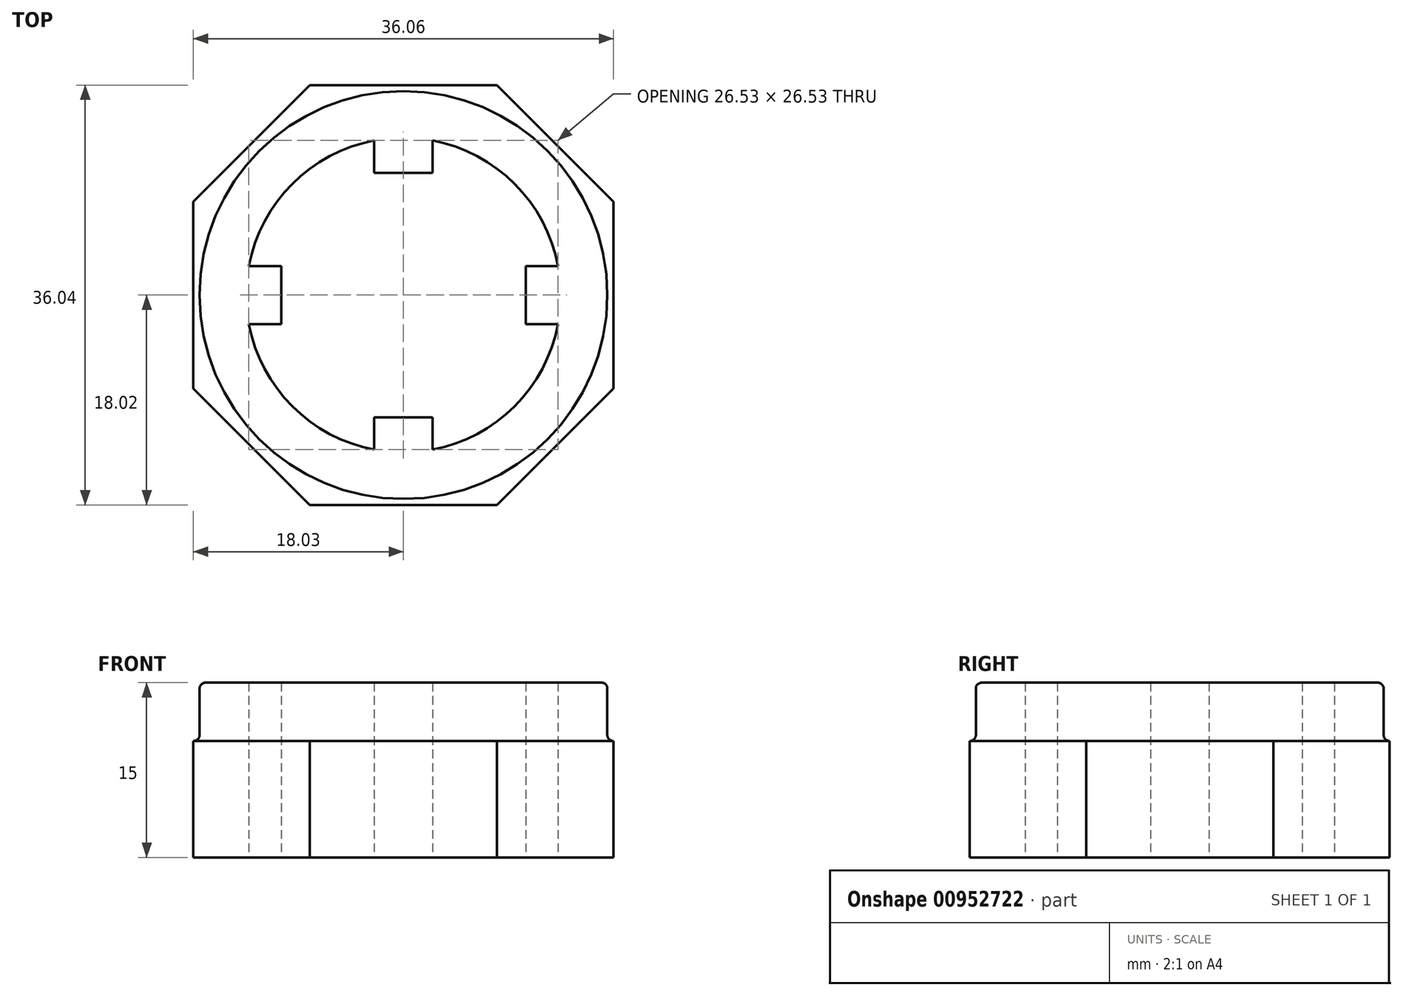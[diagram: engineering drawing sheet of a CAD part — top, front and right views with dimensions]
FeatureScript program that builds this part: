
annotation { "Feature Type Name" : "Feature", "Feature Type Description" : "" }
export const myFeature = defineFeature(function(context is Context, id is Id, definition is map)
    precondition{}
    {
        {
            var Q0;
            Q0=qCreatedBy(makeId("Top.planeOp"),FACE);
            var sketch = newSketch(context, id + "F0", { "sketchPlane" : qUnion([Q0])});
            skCircle(sketch, "E0", {"center": v(0, 0) * mm, "radius": 13.5 * mm});
            skSolve(sketch);
        }
        {
            var Q0;
            Q0=makeQuery(id+"F0.imprint","IMPRINT",FACE,{"disambiguationData":[TD([[makeQuery(id+"F0.imprint","IMPRINT",EDGE,{"derivedFrom":sQuery(id+"F0.wireOp",EDGE,"E0")}),1.0]])]});
            var sketch = newSketch(context, id + "F1", { "sketchPlane" : qUnion([Q0])});
            skCircle(sketch, "E1", {"center": v(0, 0) * mm, "radius": 17.5 * mm});
            skSolve(sketch);
        }
        {
            var Q0;
            Q0=makeQuery(id+"F1.imprint","IMPRINT",FACE,{"disambiguationData":[TD([[makeQuery(id+"F1.imprint","IMPRINT",EDGE,{"derivedFrom":sQuery(id+"F1.wireOp",EDGE,"E1")}),1.0]])]});
            var Q1;
            Q1=sQuery(id+"F1.wireOp",EDGE,"E1");
            extrude(context, id + "F2", {"entities" : qUnion([Q0]), "surfaceEntities" : qUnion([Q1]), "depth" : 15 * mm, "offsetDistance" : 25 * mm});
        }
        {
            var Q0;
            Q0=makeQuery(id+"F0.imprint","IMPRINT",FACE,{"disambiguationData":[TD([[makeQuery(id+"F0.imprint","IMPRINT",EDGE,{"derivedFrom":sQuery(id+"F0.wireOp",EDGE,"E0")}),1.0]])]});
            var sketch = newSketch(context, id + "F3", { "sketchPlane" : qUnion([Q0])});
            skCircle(sketch, "E2", {"center": v(0, 0) * mm, "radius": 10.5 * mm});
            skSolve(sketch);
        }
        {
            var Q0;
            Q0=qCreatedBy(makeId("Top.planeOp"),FACE);
            var sketch = newSketch(context, id + "F4", { "sketchPlane" : qUnion([Q0])});
            skLineSegment(sketch, "E3.bottom", {"start": v(-2.5, 14.36) * mm, "end": v(2.5, 14.36) * mm});
            skLineSegment(sketch, "E3.top", {"start": v(-2.5, 10.5) * mm, "end": v(2.5, 10.5) * mm});
            skLineSegment(sketch, "E3.left", {"start": v(-2.5, 14.36) * mm, "end": v(-2.5, 10.5) * mm});
            skLineSegment(sketch, "E3.right", {"start": v(2.5, 14.36) * mm, "end": v(2.5, 10.5) * mm});
            skSolve(sketch);
        }
        {
            var Q0;
            Q0=makeQuery(id+"F4.imprint","IMPRINT",FACE,{"disambiguationData":[TD([[makeQuery(id+"F4.imprint","IMPRINT",EDGE,{"derivedFrom":sQuery(id+"F4.wireOp",EDGE,"E3.bottom")}),-1.0]])]});
            var Q1;
            Q1=sQuery(id+"F4.wireOp",EDGE,"E3.left");
            var Q2;
            Q2=sQuery(id+"F4.wireOp",EDGE,"E3.right");
            var Q3;
            Q3=sQuery(id+"F4.wireOp",EDGE,"E3.bottom");
            var Q4;
            Q4=sQuery(id+"F4.wireOp",EDGE,"E3.top");
            extrude(context, id + "F5", {"entities" : qUnion([Q0]), "operationType" : NewBodyOperationType.ADD, "surfaceEntities" : qUnion([Q1, Q2, Q3, Q4]), "depth" : 15 * mm, "offsetDistance" : 25 * mm});
        }
        {
            var Q0;
            Q0=makeQuery(id+"F2.opExtrude","SWEPT_BODY",BODY,{"disambiguationData":[OSD([sQuery(id+"F0.wireOp",EDGE,"E0"),sQuery(id+"F1.wireOp",EDGE,"E1")])]});
            var Q1;
            Q1=sQuery(id+"F3.wireOp",EDGE,"E2");
            circularPattern(context, id + "F6", {"operationType" : NewBodyOperationType.ADD, "entities" : qUnion([Q0]), "axis" : qUnion([Q1]), "angle" : 360 * degree, "instanceCount" : 4, "equalSpace" : true});
        }
        {
            var Q0;
            Q0=makeQuery(id+"F0.imprint","IMPRINT",FACE,{"disambiguationData":[TD([[makeQuery(id+"F0.imprint","IMPRINT",EDGE,{"derivedFrom":sQuery(id+"F0.wireOp",EDGE,"E0")}),1.0]])]});
            var sketch = newSketch(context, id + "F7", { "sketchPlane" : qUnion([Q0])});
            skLineSegment(sketch, "E4.bottom", {"start": v(18.03, -18.02) * mm, "end": v(-18.03, -18.02) * mm});
            skLineSegment(sketch, "E4.top", {"start": v(18.03, 18.02) * mm, "end": v(-18.03, 18.02) * mm});
            skLineSegment(sketch, "E4.left", {"start": v(18.03, -18.02) * mm, "end": v(18.03, 18.02) * mm});
            skLineSegment(sketch, "E4.right", {"start": v(-18.03, -18.02) * mm, "end": v(-18.03, 18.02) * mm});
            skPoint(sketch, "E4.middle", {"position": v(0, 0) * mm});
            skCircle(sketch, "E5", {"center": v(0, 0) * mm, "radius": 13.5 * mm});
            skSolve(sketch);
        }
        {
            var Q0;
            Q0=makeQuery(id+"F7.imprint","IMPRINT",FACE,{"disambiguationData":[TD([[makeQuery(id+"F7.imprint","IMPRINT",EDGE,{"derivedFrom":sQuery(id+"F7.wireOp",EDGE,"E4.bottom")}),-1.0]])]});
            extrude(context, id + "F8", {"entities" : qUnion([Q0]), "operationType" : NewBodyOperationType.ADD, "depth" : 10 * mm, "offsetDistance" : 25 * mm});
        }
        {
            var Q0;
            Q0=makeQuery(id+"F8.opExtrude","SWEPT_EDGE",EDGE,{"disambiguationData":[OSD([sQuery(id+"F7.wireOp",EDGE,"E4.top"),sQuery(id+"F7.wireOp",EDGE,"E4.left")])]});
            var Q1;
            Q1=makeQuery(id+"F8.opExtrude","SWEPT_EDGE",EDGE,{"disambiguationData":[OSD([sQuery(id+"F7.wireOp",EDGE,"E4.top"),sQuery(id+"F7.wireOp",EDGE,"E4.right")])]});
            var Q2;
            Q2=makeQuery(id+"F8.opExtrude","SWEPT_EDGE",EDGE,{"disambiguationData":[OSD([sQuery(id+"F7.wireOp",EDGE,"E4.bottom"),sQuery(id+"F7.wireOp",EDGE,"E4.right")])]});
            var Q3;
            Q3=makeQuery(id+"F8.opExtrude","SWEPT_EDGE",EDGE,{"disambiguationData":[OSD([sQuery(id+"F7.wireOp",EDGE,"E4.bottom"),sQuery(id+"F7.wireOp",EDGE,"E4.left")])]});
            chamfer(context, id + "F9", {"entities" : qUnion([Q0, Q1, Q2, Q3]), "width" : 10 * mm, "tangentPropagation" : true});
        }
        {
            var Q0;
            Q0=makeQuery(id+"F8.boolean.opBoolean","INTERSECT",EDGE,{"derivedFrom":[makeQuery(id+"F2.opExtrude","SWEPT_FACE",FACE,{"disambiguationData":[OSD([sQuery(id+"F1.wireOp",EDGE,"E1")])]}),makeQuery(id+"F8.opExtrude","CAP_FACE",FACE,{"disambiguationData":[OSD([sQuery(id+"F7.wireOp",EDGE,"E4.bottom"),sQuery(id+"F7.wireOp",EDGE,"E4.top"),sQuery(id+"F7.wireOp",EDGE,"E4.left"),sQuery(id+"F7.wireOp",EDGE,"E4.right"),sQuery(id+"F7.wireOp",EDGE,"E5")])],"isStart":false})]});
            fillet(context, id + "F10", {"entities" : qUnion([Q0]), "radius" : .5 * mm, "tangentPropagation" : true, "allowEdgeOverflow" : false});
        }
        {
            var Q0;
            Q0=makeQuery(id+"F2.opExtrude","CAP_EDGE",EDGE,{"disambiguationData":[OSD([sQuery(id+"F1.wireOp",EDGE,"E1")])],"isStart":false});
            fillet(context, id + "F11", {"entities" : qUnion([Q0]), "radius" : .5 * mm, "tangentPropagation" : true, "allowEdgeOverflow" : false});
        }
    });
